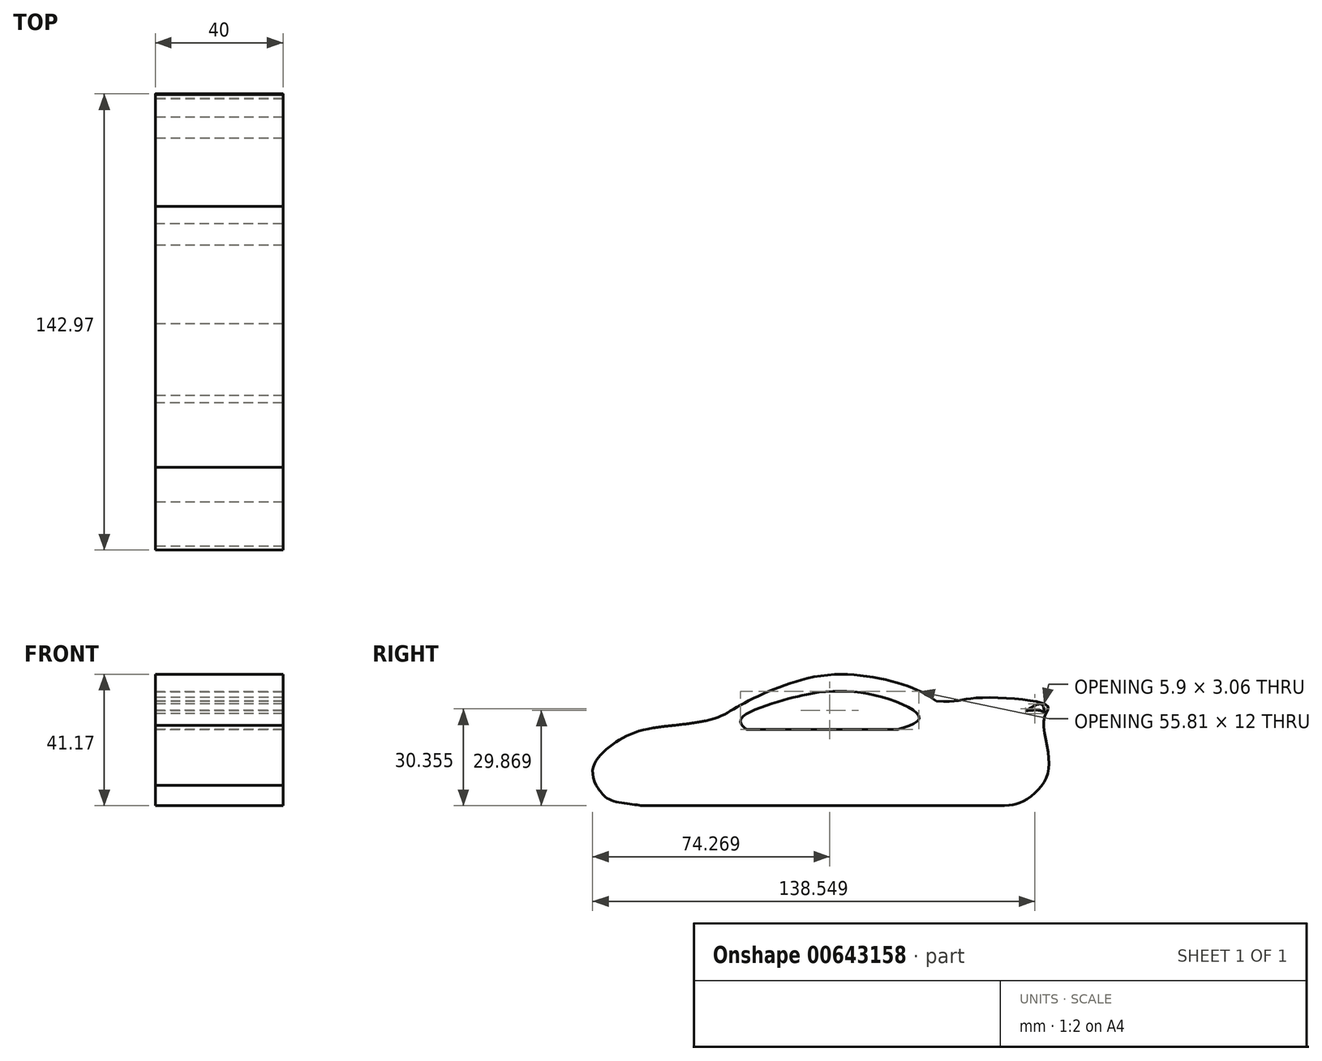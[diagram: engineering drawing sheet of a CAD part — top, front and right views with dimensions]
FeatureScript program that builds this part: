
annotation { "Feature Type Name" : "Feature", "Feature Type Description" : "" }
export const myFeature = defineFeature(function(context is Context, id is Id, definition is map)
    precondition{}
    {
        {
            var Q0;
            Q0=qCreatedBy(makeId("Right.planeOp"),FACE);
            var sketch = newSketch(context, id + "F0", { "sketchPlane" : qUnion([Q0])});
            skCircle(sketch, "E0", {"center": v(-27.33, 0) * mm, "radius": 12.5 * mm, "construction": true});
            skCircle(sketch, "E1", {"center": v(58.41, 0) * mm, "radius": 12.5 * mm, "construction": true});
            skLineSegment(sketch, "E2", {"start": v(-44.84, -6.38) * mm, "end": v(69.16, -6.38) * mm});
            skFitSpline(sketch, "E3", {"points": [v(69.16, -6.38) * mm, v(74.67, -5.21) * mm, v(80.88, 0) * mm, v(83.05, 8.45) * mm, v(81.67, 21.48) * mm, v(82.64, 24.9) * mm, v(60.3, 27.38) * mm, v(47.8, 26.46) * mm, v(-4.86, 36) * mm], "startDerivative": vector(84.6, 7.82) * mm, "endDerivative": vector(-7.85, 1.12) * mm});
            skFitSpline(sketch, "E4", {"points": [v(47.8, 26.46) * mm, v(40.26, 30.55) * mm, v(25.58, 34.27) * mm, v(6.6, 33.34) * mm, v(-14.34, 24.71) * mm, v(-24.52, 20.2) * mm, v(-60.28, 12.46) * mm], "startDerivative": vector(-64.03, 40.67) * mm, "endDerivative": vector(-88.03, -68.46) * mm});
            skFitSpline(sketch, "E5", {"points": [v(-24.52, 20.2) * mm, v(-43.36, 17.5) * mm, v(-54.57, 12.05) * mm, v(-59.85, 4.48) * mm, v(-55.07, -6.38) * mm], "startDerivative": vector(-51.9, -12.86) * mm, "endDerivative": vector(27.08, -44.46) * mm});
            skFitSpline(sketch, "E6", {"points": [v(-44.84, -6.38) * mm, v(-54.63, -4.4) * mm, v(-58.76, 0) * mm], "startDerivative": vector(-10.7, 2.98) * mm, "endDerivative": vector(-7.07, 9.73) * mm});
            skFitSpline(sketch, "E7", {"points": [v(47.8, 26.46) * mm, v(54.62, 24.05) * mm, v(67.73, 22.96) * mm, v(75.74, 23.32) * mm, v(81.67, 21.48) * mm], "startDerivative": vector(33.83, -15.67) * mm, "endDerivative": vector(-7.14, -37.2) * mm});
            skPoint(sketch, "E8.1.internal.orphan", {"position": v(82.17, 28.77) * mm});
            skFitSpline(sketch, "E9", {"points": [v(75.74, 23.32) * mm, v(80.76, 25.4) * mm, v(81.67, 21.48) * mm], "startDerivative": vector(11.31, 7.18) * mm, "endDerivative": vector(0.26, -11.32) * mm});
            skFitSpline(sketch, "E10", {"points": [v(10.98, 29.14) * mm, v(-1.82, 26.2) * mm, v(-13.6, 19.92) * mm, v(-11.5, 17.5) * mm, v(-11.46, 17.49) * mm], "startDerivative": vector(-28.93, -4.95) * mm, "endDerivative": vector(0.95, 0.46) * mm});
            skLineSegment(sketch, "E11", {"start": v(-11.46, 17.49) * mm, "end": v(21.66, 17.49) * mm});
            skLineSegment(sketch, "E12", {"start": v(21.66, 17.49) * mm, "end": v(35.7, 17.49) * mm});
            skFitSpline(sketch, "E13", {"points": [v(35.7, 17.49) * mm, v(42.33, 20.67) * mm, v(33.17, 26.95) * mm, v(10.98, 29.14) * mm], "startDerivative": vector(12.7, 5.55) * mm, "endDerivative": vector(-50.19, -5.67) * mm});
            skSolve(sketch);
        }
        {
            var Q0;
            Q0 = qSketchRegion(id + "F0", true);
            extrude(context, id + "F1", {"entities" : qUnion([Q0]), "depth" : 40 * mm, "offsetDistance" : 25 * mm});
        }
    });
